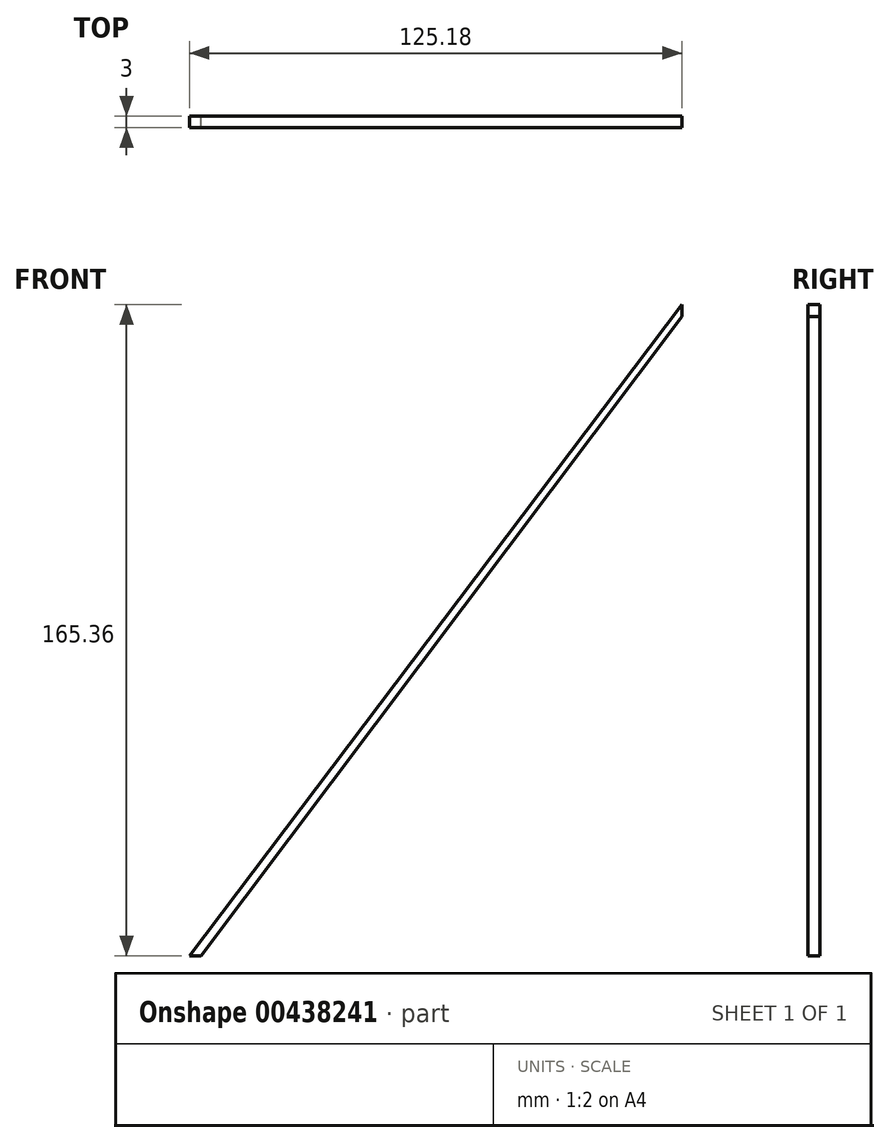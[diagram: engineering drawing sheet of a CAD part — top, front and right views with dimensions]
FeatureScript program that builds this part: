
annotation { "Feature Type Name" : "Feature", "Feature Type Description" : "" }
export const myFeature = defineFeature(function(context is Context, id is Id, definition is map)
    precondition{}
    {
        {
            var Q0;
            Q0=qCreatedBy(makeId("Front.planeOp"),FACE);
            var sketch = newSketch(context, id + "F0", { "sketchPlane" : qUnion([Q0])});
            skLineSegment(sketch, "E0", {"start": v(-56.23, -25.7) * mm, "end": v(-53.23, -25.7) * mm});
            skLineSegment(sketch, "E1", {"start": v(-53.23, -25.7) * mm, "end": v(68.95, 136.66) * mm});
            skLineSegment(sketch, "E2", {"start": v(68.95, 136.66) * mm, "end": v(68.95, 139.66) * mm});
            skLineSegment(sketch, "E3", {"start": v(68.95, 139.66) * mm, "end": v(-56.23, -25.7) * mm});
            skSolve(sketch);
        }
        {
            var Q0;
            Q0 = qSketchRegion(id + "F0", true);
            extrude(context, id + "F1", {"entities" : qUnion([Q0]), "depth" : 3 * mm});
        }
    });
